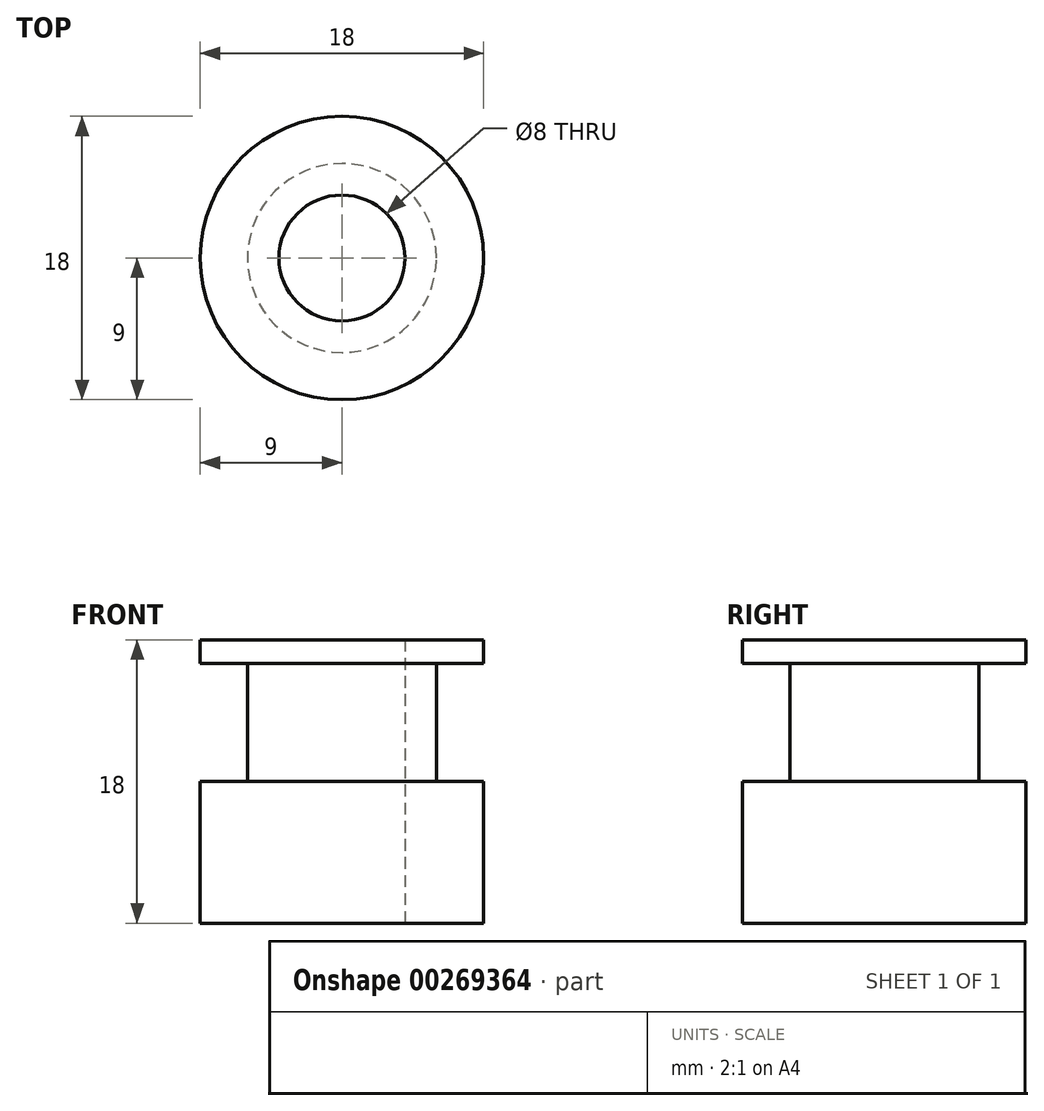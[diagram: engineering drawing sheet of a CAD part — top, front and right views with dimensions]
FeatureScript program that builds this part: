
annotation { "Feature Type Name" : "Feature", "Feature Type Description" : "" }
export const myFeature = defineFeature(function(context is Context, id is Id, definition is map)
    precondition{}
    {
        {
            var Q0;
            Q0=qCreatedBy(makeId("Top.planeOp"),FACE);
            var sketch = newSketch(context, id + "F0", { "sketchPlane" : qUnion([Q0])});
            skCircle(sketch, "E0", {"center": v(0, 0) * mm, "radius": 9 * mm});
            skCircle(sketch, "E1", {"center": v(0, 0) * mm, "radius": 4 * mm});
            skSolve(sketch);
        }
        {
            var Q0;
            Q0=makeQuery(id+"F0.imprint","IMPRINT",FACE,{"disambiguationData":[TD([[makeQuery(id+"F0.imprint","IMPRINT",EDGE,{"derivedFrom":sQuery(id+"F0.wireOp",EDGE,"E0")}),1.0]])]});
            extrude(context, id + "F1", {"entities" : qUnion([Q0]), "depth" : 9 * mm});
        }
        {
            var Q0;
            Q0=makeQuery(id+"F1.opExtrude","CAP_FACE",FACE,{"disambiguationData":[OSD([sQuery(id+"F0.wireOp",EDGE,"E0"),sQuery(id+"F0.wireOp",EDGE,"E1")])],"isStart":false});
            var sketch = newSketch(context, id + "F2", { "sketchPlane" : qUnion([Q0])});
            skCircle(sketch, "E2", {"center": v(0, 0) * mm, "radius": 6 * mm});
            skSolve(sketch);
        }
        {
            var Q0;
            Q0=makeQuery(id+"F2.imprint","IMPRINT",FACE,{"disambiguationData":[TD([[makeQuery(id+"F2.imprint","IMPRINT",EDGE,{"derivedFrom":sQuery(id+"F2.wireOp",EDGE,"E2")}),1.0]])]});
            extrude(context, id + "F3", {"entities" : qUnion([Q0]), "operationType" : NewBodyOperationType.ADD, "depth" : 7.5 * mm});
        }
        {
            var Q0;
            Q0=makeQuery(id+"F3.opExtrude","CAP_FACE",FACE,{"disambiguationData":[OSD([sQuery(id+"F0.wireOp",EDGE,"E1"),sQuery(id+"F2.wireOp",EDGE,"E2")])],"isStart":false});
            var sketch = newSketch(context, id + "F4", { "sketchPlane" : qUnion([Q0])});
            skCircle(sketch, "E3.0", {"center": v(0, 0) * mm, "radius": 9 * mm});
            skSolve(sketch);
        }
        {
            var Q0;
            Q0=makeQuery(id+"F4.imprint","IMPRINT",FACE,{"disambiguationData":[TD([[makeQuery(id+"F4.imprint","IMPRINT",EDGE,{"derivedFrom":sQuery(id+"F4.wireOp",EDGE,"E3.0")}),1.0]])]});
            var Q1;
            Q1=makeQuery(id+"F4.imprint","IMPRINT",FACE,{"disambiguationData":[TD([[makeQuery(id+"F4.imprint","IMPRINT",EDGE,{"derivedFrom":makeQuery(id+"F3.opExtrude","CAP_EDGE",EDGE,{"disambiguationData":[OSD([sQuery(id+"F2.wireOp",EDGE,"E2")])],"isStart":false})}),1.0]])]});
            extrude(context, id + "F5", {"entities" : qUnion([Q0, Q1]), "operationType" : NewBodyOperationType.ADD, "depth" : 1.5 * mm});
        }
    });
